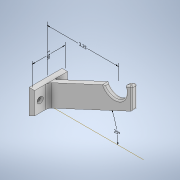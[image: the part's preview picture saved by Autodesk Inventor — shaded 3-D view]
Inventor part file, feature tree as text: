
AUTODESK INVENTOR PART (.ipt)
format: ipt  version: 2021.1 (Build 251245010, 245A)  size: 413,184 bytes
history: native  units: in
note: dims shown in document units (in); Inventor stores cm internally (conversion verified against a paired STEP export)
features: sketch x5, other x4, extrude x4, fillet x4, hole x1
ambient origin geometry x8: Origin, YZ Plane, XZ Plane, XY Plane, X Axis, Y Axis, Z Axis, Center Point
bodies: Solid2 (feature_tree)
feature tree (18):
  other  "Annotations"
  extrude  "Extrusion3"  Depth=0.25in
  extrude  "Extrusion4"  Depth=0.1718in
  sketch  "Sketch7"  dims[d26=1.075in d29=0.25in]
  extrude  "Extrusion5"  Depth=0.25in
  hole  "Hole3"  [1 undecoded]
  fillet  "Fillet3"  [1 undecoded]
  fillet  "Fillet4"  [1 undecoded]
  fillet  "Fillet5"  Radius=0.25in
  fillet  "Fillet6"  Radius=0.25in
  extrude  "Extrusion6"  Depth=0.0625in
  sketch  "Sketch5"  dims[d21=1.0in d22=0.25in]
  sketch  "Sketch6"  dims[d23=1.5in d24=0.0in d25=0.1718in]
  sketch  "Sketch8"  dims[d30=3.25in d31=0.25in d32=0.0in d33=0.0in d34=0.25in d35=0.25in]
  sketch  "Sketch9"  dims[d47=1.5in d48=0.0in d49=0.15in d50=0.75in d51=0.279in d52=0.25in d53=0.5635in d54=1.0in d55=0.8108in d65=0.0625in d66=0.0625in d67=0.0625in d68=0.125in d70=0.05in d71=0.0in d56=0.2085in d57=0.331in d58=1.5in d59=2.3174in d60=0.1718in d69=3.25in]
  other  "Linear Dimension 1"
  other  "Angular Dimension 1"
  other  "Linear Dimension 2"
note: 3 required parameter values undecoded (feature->parameter linkage not recoverable at this tier; creation-order binding heuristic only, values carry confidence <= 0.55)
